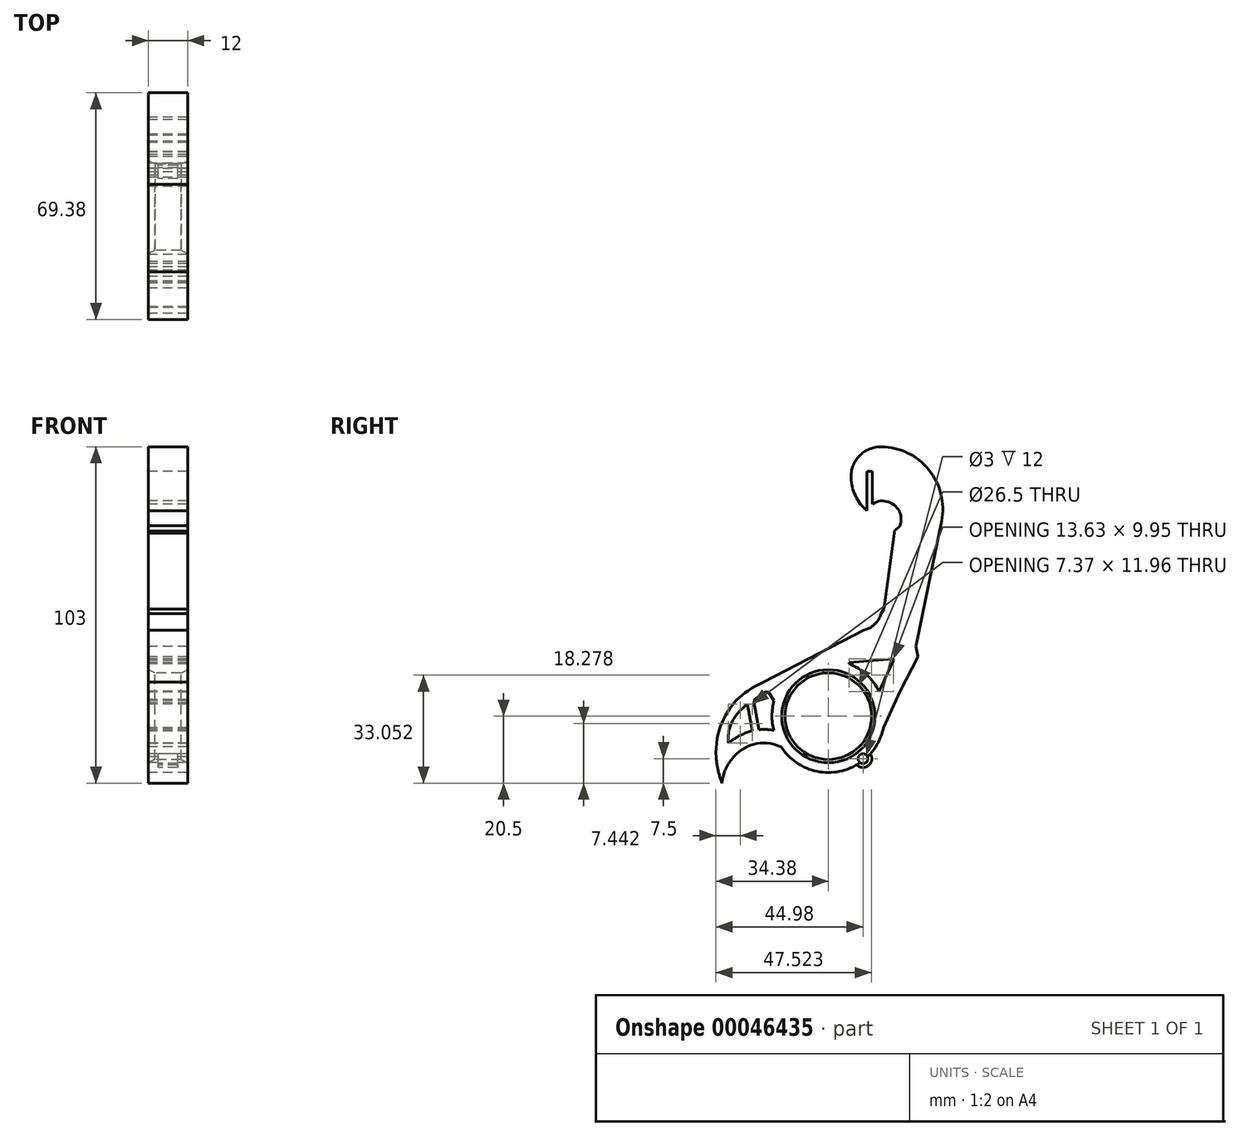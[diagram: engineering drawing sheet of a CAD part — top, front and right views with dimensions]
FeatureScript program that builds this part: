
annotation { "Feature Type Name" : "Feature", "Feature Type Description" : "" }
export const myFeature = defineFeature(function(context is Context, id is Id, definition is map)
    precondition{}
    {
        {
            var Q0;
            Q0=qCreatedBy(makeId("Right.planeOp"),FACE);
            var sketch = newSketch(context, id + "F0", { "sketchPlane" : qUnion([Q0])});
            skLineSegment(sketch, "E0", {"start": v(34.62, 28.72) * mm, "end": v(26.84, -9.58) * mm});
            skLineSegment(sketch, "E1", {"start": v(26.84, -9.58) * mm, "end": v(27.49, -12.78) * mm});
            skLineSegment(sketch, "E2", {"start": v(27.49, -12.78) * mm, "end": v(21.97, -23.3) * mm});
            skLineSegment(sketch, "E3", {"start": v(21.97, -23.3) * mm, "end": v(16.87, -34.58) * mm});
            skPoint(sketch, "E4", {"position": v(0, -31) * mm});
            skCircle(sketch, "E5", {"center": v(0, -31) * mm, "radius": 13.25 * mm});
            skLineSegment(sketch, "E6", {"start": v(19.78, -13.47) * mm, "end": v(19.96, -13.94) * mm});
            skLineSegment(sketch, "E7", {"start": v(19.96, -13.94) * mm, "end": v(15.5, -23.42) * mm});
            skCircle(sketch, "E8.0", {"center": v(0, -31) * mm, "radius": 17.25 * mm});
            skLineSegment(sketch, "E9", {"start": v(19.78, -13.47) * mm, "end": v(6.38, -14.56) * mm});
            skLineSegment(sketch, "E10", {"start": v(6.38, -14.56) * mm, "end": v(6.33, -14.95) * mm});
            skArc(sketch, "E11", {"start": v(34.62, 28.72) * mm, "mid": v(30.78, 44.44) * mm, "end": v(16.2, 51.5) * mm});
            skArc(sketch, "E12", {"start": v(16.2, 51.5) * mm, "mid": v(9.53, 48.73) * mm, "end": v(6.94, 41.98) * mm});
            skArc(sketch, "E13", {"start": v(6.94, 41.98) * mm, "mid": v(8.31, 36.42) * mm, "end": v(11.8, 31.88) * mm});
            skLineSegment(sketch, "E14", {"start": v(11.8, 31.88) * mm, "end": v(11.8, 43.9) * mm});
            skLineSegment(sketch, "E15", {"start": v(11.8, 43.9) * mm, "end": v(13.5, 43.9) * mm});
            skLineSegment(sketch, "E16", {"start": v(13.5, 43.9) * mm, "end": v(13.5, 33.9) * mm});
            skLineSegment(sketch, "E17", {"start": v(10.76, -4.62) * mm, "end": v(-19.86, -20.61) * mm});
            skPoint(sketch, "E18", {"position": v(10.6, -44) * mm});
            skCircle(sketch, "E19", {"center": v(10.6, -44) * mm, "radius": 1.5 * mm});
            skCircle(sketch, "E20.0", {"center": v(10.6, -44) * mm, "radius": 2.7 * mm});
            skPoint(sketch, "E21", {"position": v(-18, -54) * mm});
            skFitSpline(sketch, "E22", {"points": [v(-14.5, -40.33) * mm, v(-25.71, -40.8) * mm, v(-32.54, -51.5) * mm], "startDerivative": vector(-24.93, 10.52) * mm, "endDerivative": vector(-3.38, -29.54) * mm});
            skFitSpline(sketch, "E23", {"points": [v(-19.86, -20.61) * mm, v(-31.36, -30.6) * mm, v(-32.54, -51.5) * mm], "startDerivative": vector(-36.87, -16.6) * mm, "endDerivative": vector(18.31, -48.4) * mm});
            skFitSpline(sketch, "E24", {"points": [v(13.5, 33.9) * mm, v(20.55, 33.3) * mm, v(21.91, 27.3) * mm], "startDerivative": vector(13.09, 10.47) * mm, "endDerivative": vector(-4.9, -14.1) * mm});
            skLineSegment(sketch, "E25", {"start": v(21.91, 27.3) * mm, "end": v(20.16, 25.7) * mm});
            skLineSegment(sketch, "E26", {"start": v(20.16, 25.7) * mm, "end": v(20.16, 25.01) * mm});
            skLineSegment(sketch, "E27", {"start": v(20.16, 25.01) * mm, "end": v(17, 1.82) * mm});
            skLineSegment(sketch, "E28", {"start": v(17, 1.82) * mm, "end": v(16.16, 0.4) * mm});
            skFitSpline(sketch, "E29", {"points": [v(16.16, 0.4) * mm, v(13.98, -3.03) * mm, v(10.76, -4.62) * mm], "startDerivative": vector(-3.68, -10.82) * mm, "endDerivative": vector(-9.88, -2.16) * mm});
            skFitSpline(sketch, "E30.0", {"points": [v(-12.95, -36.65) * mm, v(-14.25, -36.1) * mm, v(-16.9, -35.31) * mm, v(-20.87, -35.1) * mm, v(-24.04, -35.7) * mm, v(-26.41, -36.62) * mm, v(-28.1, -37.5) * mm, v(-29.69, -38.59) * mm, v(-31.66, -40.28) * mm, v(-33.8, -42.86) * mm, v(-35.66, -46.63) * mm, v(-36.34, -49.52) * mm, v(-36.51, -51.04) * mm]});
            skLineSegment(sketch, "E31", {"start": v(-16.6, -26.3) * mm, "end": v(-18.3, -23.58) * mm});
            skLineSegment(sketch, "E32", {"start": v(-18.3, -23.58) * mm, "end": v(-19.29, -23.45) * mm});
            skLineSegment(sketch, "E33", {"start": v(-19.29, -23.45) * mm, "end": v(-22.64, -25.92) * mm});
            skLineSegment(sketch, "E34", {"start": v(-22.64, -25.92) * mm, "end": v(-22.79, -26.9) * mm});
            skLineSegment(sketch, "E35", {"start": v(-22.79, -26.9) * mm, "end": v(-21.22, -35.29) * mm});
            skFitSpline(sketch, "E36", {"points": [v(-24.79, -27.24) * mm, v(-29.38, -32.58) * mm, v(-30.45, -39.26) * mm], "startDerivative": vector(-10.6, -9.75) * mm, "endDerivative": vector(2.7, -12.29) * mm});
            skLineSegment(sketch, "E37", {"start": v(-24.79, -27.24) * mm, "end": v(-23.23, -35.6) * mm});
            skSolve(sketch);
        }
        {
            var Q0;
            Q0=makeQuery(id+"F0.imprint","IMPRINT",FACE,{"disambiguationData":[TD([[makeQuery(id+"F0.imprint","IMPRINT",EDGE,{"derivedFrom":sQuery(id+"F0.wireOp",EDGE,"E0")}),-1.0]])]});
            var Q1;
            Q1=makeQuery(id+"F0.imprint","IMPRINT",FACE,{"disambiguationData":[TD([[makeQuery(id+"F0.imprint","IMPRINT",EDGE,{"derivedFrom":sQuery(id+"F0.wireOp",EDGE,"E5")}),-1.0]])]});
            var Q2;
            {var subQ0=sQuery(id+"F0.wireOp",EDGE,"E20.0");var subQ1=sQuery(id+"F0.wireOp",EDGE,"E8.0");var subQ2=makeQuery(id+"F0.imprint","INTERSECT",VERTEX,{"disambiguationData":[OD(0.0)],"derivedFrom":[subQ1,subQ0]});Q2=makeQuery(id+"F0.imprint","IMPRINT",FACE,{"disambiguationData":[TD([[makeQuery(id+"F0.imprint","IMPRINT",EDGE,{"disambiguationData":[TD([[subQ2,-1.0]])],"derivedFrom":subQ1}),1.0]])]});}
            var Q3;
            {var subQ5=sQuery(id+"F0.wireOp",EDGE,"E22");Q3=makeQuery(id+"F0.imprint","IMPRINT",FACE,{"disambiguationData":[TD([[makeQuery(id+"F0.imprint","IMPRINT",EDGE,{"derivedFrom":subQ5}),-1.0]])]});}
            extrude(context, id + "F1", {"entities" : qUnion([Q0, Q1, Q2, Q3]), "depth" : 12 * mm, "offsetDistance" : 25 * mm, "symmetric" : true});
        }
        {
            var Q0;
            Q0=makeQuery(id+"F1.opExtrude","CAP_EDGE",EDGE,{"disambiguationData":[OSD([sQuery(id+"F0.wireOp",EDGE,"E5")])],"isStart":true});
            var Q1;
            Q1=makeQuery(id+"F1.opExtrude","CAP_EDGE",EDGE,{"disambiguationData":[OSD([sQuery(id+"F0.wireOp",EDGE,"E5")])],"isStart":false});
            chamfer(context, id + "F2", {"entities" : qUnion([Q0, Q1]), "chamferType" : ChamferType.TWO_OFFSETS, "width1" : 1 * mm, "oppositeDirection" : false, "width2" : 2 * mm, "tangentPropagation" : true});
        }
        {
            var Q0;
            {var subQ0=sQuery(id+"F0.wireOp",EDGE,"E20.0");var subQ1=sQuery(id+"F0.wireOp",EDGE,"E8.0");var subQ2=makeQuery(id+"F0.imprint","INTERSECT",VERTEX,{"disambiguationData":[OD(0.0)],"derivedFrom":[subQ1,subQ0]});Q0=makeQuery(id+"F0.imprint","IMPRINT",FACE,{"disambiguationData":[TD([[makeQuery(id+"F0.imprint","IMPRINT",EDGE,{"disambiguationData":[TD([[subQ2,-1.0]])],"derivedFrom":subQ1}),-1.0]])]});}
            extrude(context, id + "F3", {"entities" : qUnion([Q0]), "operationType" : NewBodyOperationType.ADD, "depth" : 6 * mm, "offsetDistance" : 25 * mm, "symmetric" : true});
        }
    });
